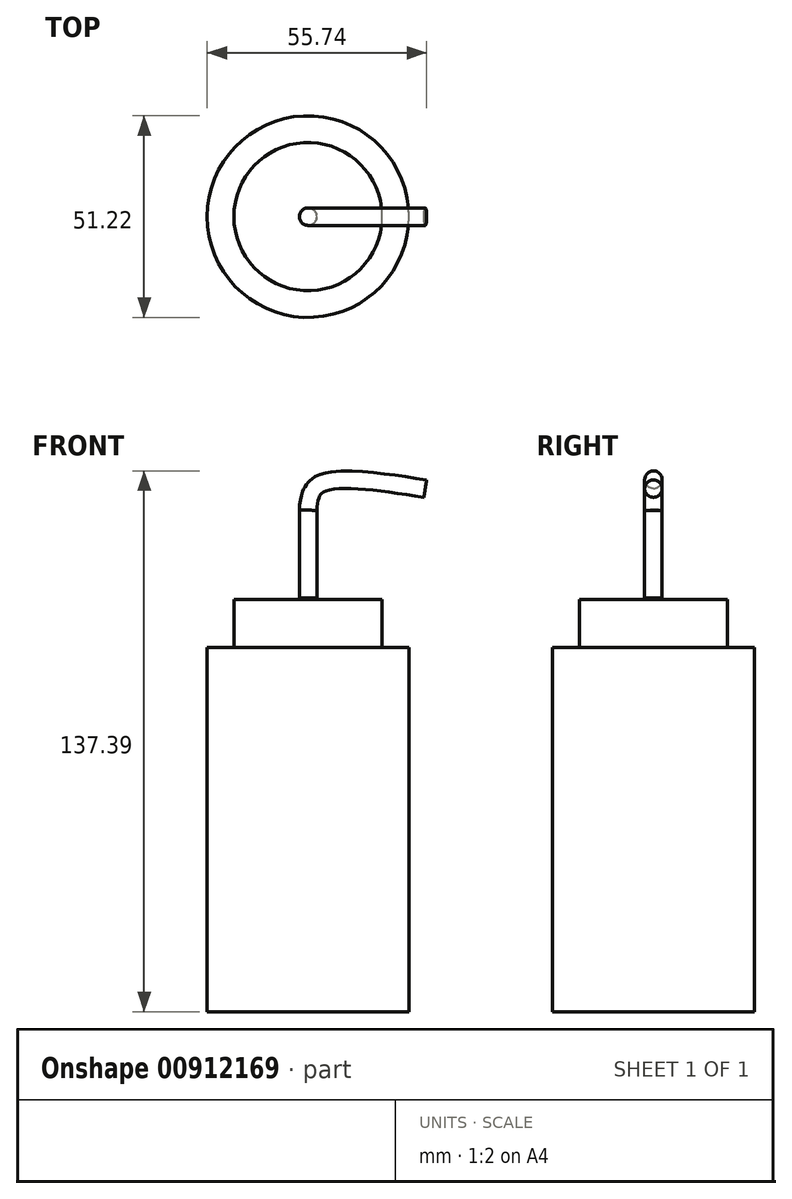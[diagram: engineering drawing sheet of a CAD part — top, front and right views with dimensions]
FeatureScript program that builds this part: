
annotation { "Feature Type Name" : "Feature", "Feature Type Description" : "" }
export const myFeature = defineFeature(function(context is Context, id is Id, definition is map)
    precondition{}
    {
        {
            var Q0;
            Q0=qCreatedBy(makeId("Right.planeOp"),FACE);
            var sketch = newSketch(context, id + "F0", { "sketchPlane" : qUnion([Q0])});
            skLineSegment(sketch, "E0", {"start": v(0, -61.95) * mm, "end": v(25.61, -61.95) * mm});
            skLineSegment(sketch, "E1", {"start": v(25.61, -61.95) * mm, "end": v(25.61, 30.57) * mm});
            skLineSegment(sketch, "E2", {"start": v(25.61, 30.57) * mm, "end": v(0, 30.57) * mm});
            skLineSegment(sketch, "E3", {"start": v(0, 30.57) * mm, "end": v(0, -61.95) * mm});
            skLineSegment(sketch, "E4", {"start": v(18.83, 30.57) * mm, "end": v(18.83, 42.77) * mm});
            skLineSegment(sketch, "E5", {"start": v(18.83, 42.77) * mm, "end": v(0, 42.77) * mm});
            skLineSegment(sketch, "E6", {"start": v(0, 42.77) * mm, "end": v(0, 30.57) * mm});
            skLineSegment(sketch, "E7", {"start": v(0, 42.77) * mm, "end": v(0, -61.95) * mm, "construction": true});
            skSolve(sketch);
        }
        {
            var Q0;
            Q0=makeQuery(id+"F0.imprint","IMPRINT",FACE,{"disambiguationData":[TD([[makeQuery(id+"F0.imprint","IMPRINT",EDGE,{"derivedFrom":sQuery(id+"F0.wireOp",EDGE,"E0")}),1.0]])]});
            var Q1;
            {var subQ2=sQuery(id+"F0.wireOp",EDGE,"E4");Q1=makeQuery(id+"F0.imprint","IMPRINT",FACE,{"disambiguationData":[TD([[makeQuery(id+"F0.imprint","IMPRINT",EDGE,{"derivedFrom":subQ2}),1.0]])]});}
            var Q2;
            Q2=sQuery(id+"F0.wireOp",EDGE,"E3");
            revolve(context, id + "F1", {"surfaceOperationType" : NewSurfaceOperationType.NEW, "entities" : qUnion([Q0, Q1]), "axis" : qUnion([Q2]), "revolveType" : RevolveType.FULL});
        }
        {
            var Q0;
            Q0=qCreatedBy(makeId("Front.planeOp"),FACE);
            var sketch = newSketch(context, id + "F2", { "sketchPlane" : qUnion([Q0])});
            skFitSpline(sketch, "E8", {"points": [v(0, 43.1) * mm, v(0, 65.49) * mm], "startDerivative": vector(0, 22.39) * mm, "endDerivative": vector(0, 22.39) * mm});
            skFitSpline(sketch, "E9", {"points": [v(0, 65.49) * mm, v(2.55, 71.83) * mm, v(29.79, 70.93) * mm], "startDerivative": vector(2.1, 22.4) * mm, "endDerivative": vector(51.95, -8.14) * mm});
            skSolve(sketch);
        }
        {
            var Q0;
            Q0=sQuery(id+"F2.wireOp",VERTEX,"E9.end");
            var Q1;
            Q1=sQuery(id+"F2.wireOp",EDGE,"E9");
            cPlane(context, id + "F3", {"entities" : qUnion([Q0, Q1]), "cplaneType" : CPlaneType.CURVE_POINT, "offset" : 25.4 * mm, "width" : 152.4 * mm, "height" : 152.4 * mm});
        }
        {
            var Q0;
            Q0=qCreatedBy(id+"F3.planeOp",FACE);
            var sketch = newSketch(context, id + "F4", { "sketchPlane" : qUnion([Q0])});
            skCircle(sketch, "E10", {"center": v(0, 74.68) * mm, "radius": 2.22 * mm});
            skSolve(sketch);
        }
        {
            var Q0;
            Q0=makeQuery(id+"F4.imprint","IMPRINT",FACE,{"disambiguationData":[TD([[makeQuery(id+"F4.imprint","IMPRINT",EDGE,{"derivedFrom":sQuery(id+"F4.wireOp",EDGE,"E10")}),1.0]])]});
            var Q1;
            Q1=sQuery(id+"F2.wireOp",EDGE,"E9");
            var Q2;
            Q2=sQuery(id+"F2.wireOp",EDGE,"E8");
            sweep(context, id + "F5", {"profiles" : qUnion([Q0]), "path" : qUnion([Q1, Q2])});
        }
    });
